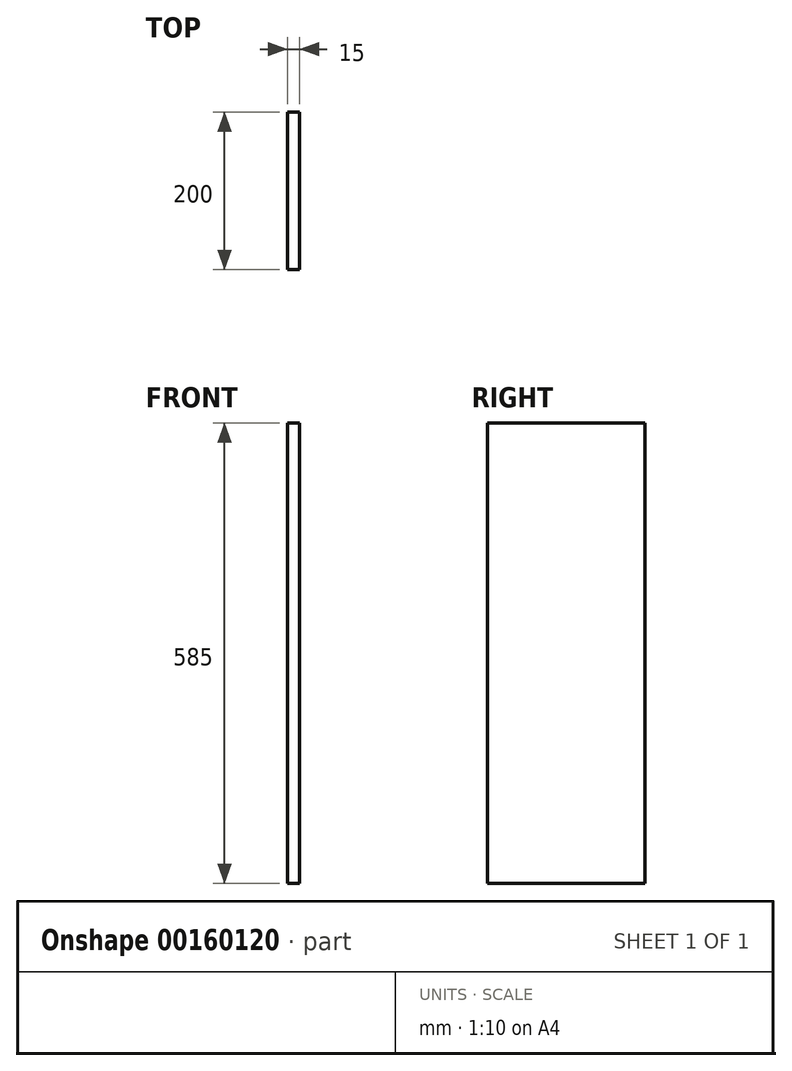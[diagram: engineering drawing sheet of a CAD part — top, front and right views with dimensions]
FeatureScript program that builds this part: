
annotation { "Feature Type Name" : "Feature", "Feature Type Description" : "" }
export const myFeature = defineFeature(function(context is Context, id is Id, definition is map)
    precondition{}
    {
        {
            var Q0;
            Q0=qCreatedBy(makeId("Right.planeOp"),FACE);
            var sketch = newSketch(context, id + "F0", { "sketchPlane" : qUnion([Q0])});
            skLineSegment(sketch, "E0.bottom", {"start": v(-41.27, 542.32) * mm, "end": v(158.73, 542.32) * mm});
            skLineSegment(sketch, "E0.top", {"start": v(-41.27, -42.68) * mm, "end": v(158.73, -42.68) * mm});
            skLineSegment(sketch, "E0.left", {"start": v(-41.27, 542.32) * mm, "end": v(-41.27, -42.68) * mm});
            skLineSegment(sketch, "E0.right", {"start": v(158.73, 542.32) * mm, "end": v(158.73, -42.68) * mm});
            skSolve(sketch);
        }
        {
            var Q0;
            Q0=makeQuery(id+"F0.imprint","IMPRINT",FACE,{"disambiguationData":[TD([[makeQuery(id+"F0.imprint","IMPRINT",EDGE,{"derivedFrom":sQuery(id+"F0.wireOp",EDGE,"E0.bottom")}),-1.0]])]});
            extrude(context, id + "F1", {"entities" : qUnion([Q0]), "depth" : 15 * mm});
        }
    });
